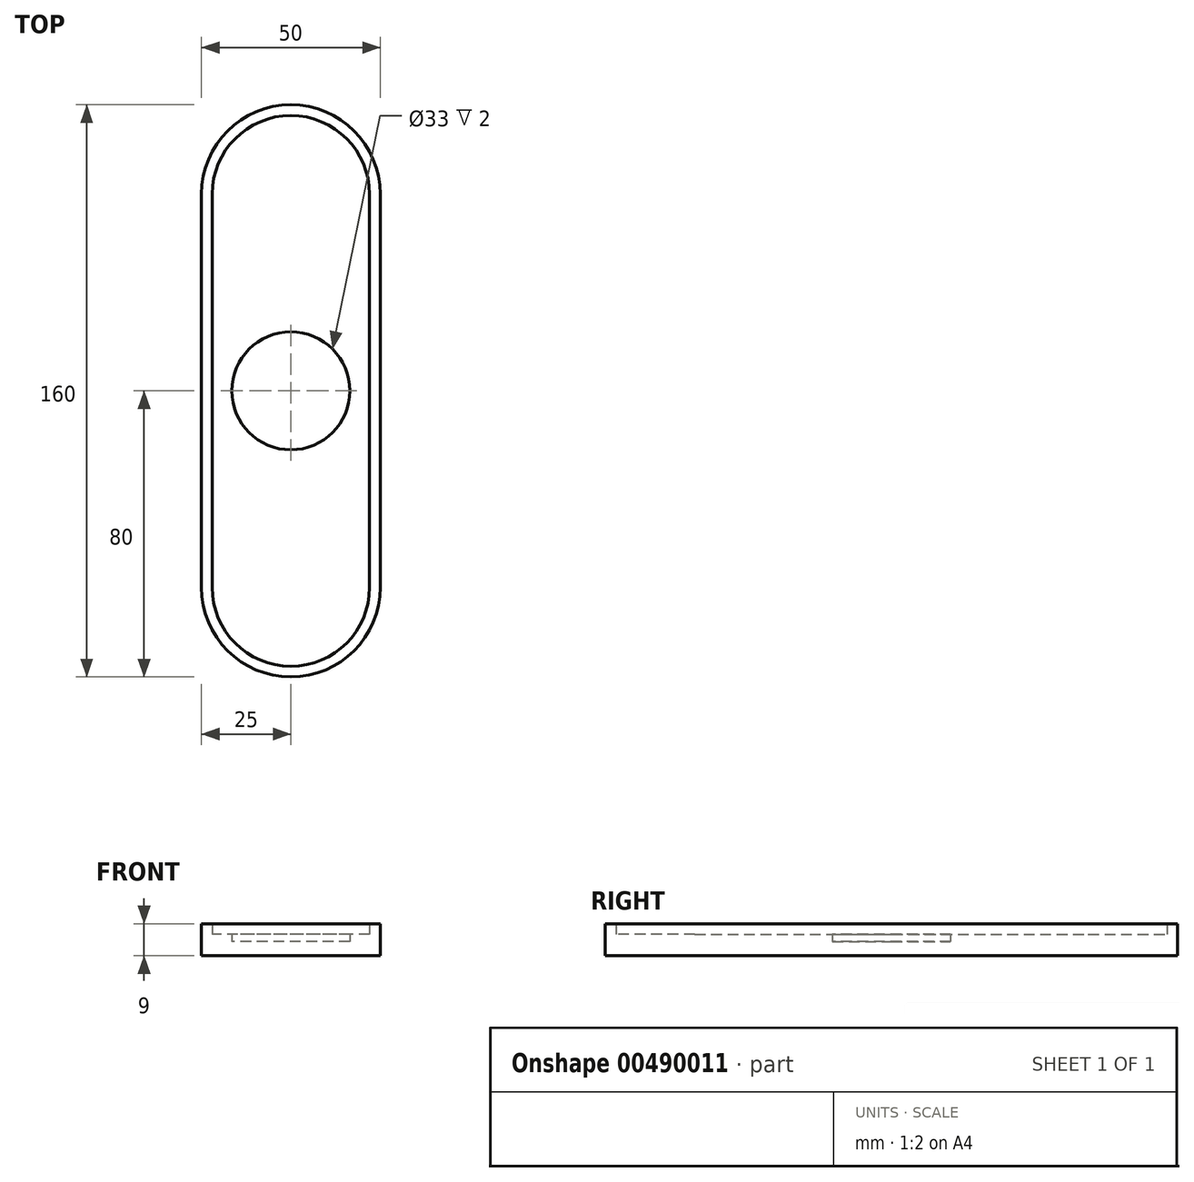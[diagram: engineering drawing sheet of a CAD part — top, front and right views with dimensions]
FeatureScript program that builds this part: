
annotation { "Feature Type Name" : "Feature", "Feature Type Description" : "" }
export const myFeature = defineFeature(function(context is Context, id is Id, definition is map)
    precondition{}
    {
        {
            var Q0;
            Q0=qCreatedBy(makeId("Top.planeOp"),FACE);
            var sketch = newSketch(context, id + "F0", { "sketchPlane" : qUnion([Q0])});
            skLineSegment(sketch, "E0.bottom", {"start": v(0, -80) * mm, "end": v(0, -80) * mm});
            skLineSegment(sketch, "E0.top", {"start": v(0, 80) * mm, "end": v(0, 80) * mm});
            skLineSegment(sketch, "E0.left", {"start": v(25, -55) * mm, "end": v(25, 55) * mm});
            skLineSegment(sketch, "E0.right", {"start": v(-25, -55) * mm, "end": v(-25, 55) * mm});
            skPoint(sketch, "E0.middle", {"position": v(0, 0) * mm});
            skLineSegment(sketch, "E1.0", {"start": v(0, 77) * mm, "end": v(0, 77) * mm});
            skLineSegment(sketch, "E1.1", {"start": v(22, -55) * mm, "end": v(22, 55) * mm});
            skLineSegment(sketch, "E1.2", {"start": v(0, -77) * mm, "end": v(0, -77) * mm});
            skLineSegment(sketch, "E1.3", {"start": v(-22, -55) * mm, "end": v(-22, 55) * mm});
            skCircle(sketch, "E2", {"center": v(0, 0) * mm, "radius": 16.5 * mm});
            skCircle(sketch, "E3.1.0.0", {"center": v(0, 45) * mm, "radius": 16.5 * mm});
            skLineSegment(sketch, "E3.direction1", {"start": v(0, 0) * mm, "end": v(0, 45) * mm, "construction": true});
            skCircle(sketch, "E4", {"center": v(0, -45) * mm, "radius": 15 * mm});
            skPoint(sketch, "E5.visualSharp", {"position": v(-22, 77) * mm});
            skArc(sketch, "E5.filletArc", {"start": v(0, 77) * mm, "mid": v(-15.56, 70.56) * mm, "end": v(-22, 55) * mm});
            skPoint(sketch, "E6.visualSharp", {"position": v(22, 77) * mm});
            skArc(sketch, "E6.filletArc", {"start": v(22, 55) * mm, "mid": v(15.56, 70.56) * mm, "end": v(0, 77) * mm});
            skPoint(sketch, "E7.visualSharp", {"position": v(-22, -77) * mm});
            skArc(sketch, "E7.filletArc", {"start": v(-22, -55) * mm, "mid": v(-15.56, -70.56) * mm, "end": v(0, -77) * mm});
            skPoint(sketch, "E8.visualSharp", {"position": v(22, -77) * mm});
            skArc(sketch, "E8.filletArc", {"start": v(0, -77) * mm, "mid": v(15.56, -70.56) * mm, "end": v(22, -55) * mm});
            skPoint(sketch, "E9.visualSharp", {"position": v(-25, 80) * mm});
            skArc(sketch, "E9.filletArc", {"start": v(0, 80) * mm, "mid": v(-17.68, 72.68) * mm, "end": v(-25, 55) * mm});
            skPoint(sketch, "E10.visualSharp", {"position": v(25, 80) * mm});
            skArc(sketch, "E10.filletArc", {"start": v(25, 55) * mm, "mid": v(17.68, 72.68) * mm, "end": v(0, 80) * mm});
            skPoint(sketch, "E11.visualSharp", {"position": v(-25, -80) * mm});
            skArc(sketch, "E11.filletArc", {"start": v(-25, -55) * mm, "mid": v(-17.68, -72.68) * mm, "end": v(0, -80) * mm});
            skPoint(sketch, "E12.visualSharp", {"position": v(25, -80) * mm});
            skArc(sketch, "E12.filletArc", {"start": v(0, -80) * mm, "mid": v(17.68, -72.68) * mm, "end": v(25, -55) * mm});
            skSolve(sketch);
        }
        {
            var Q0;
            Q0=makeQuery(id+"F0.imprint","IMPRINT",FACE,{"disambiguationData":[TD([[makeQuery(id+"F0.imprint","IMPRINT",EDGE,{"derivedFrom":sQuery(id+"F0.wireOp",EDGE,"E1.1")}),1.0]])]});
            var Q1;
            Q1=makeQuery(id+"F0.imprint","IMPRINT",FACE,{"disambiguationData":[TD([[makeQuery(id+"F0.imprint","IMPRINT",EDGE,{"derivedFrom":sQuery(id+"F0.wireOp",EDGE,"E4")}),1.0]])]});
            var Q2;
            Q2=makeQuery(id+"F0.imprint","IMPRINT",FACE,{"disambiguationData":[TD([[makeQuery(id+"F0.imprint","IMPRINT",EDGE,{"derivedFrom":sQuery(id+"F0.wireOp",EDGE,"E3.1.0.0")}),1.0]])]});
            extrude(context, id + "F1", {"entities" : qUnion([Q0, Q1, Q2]), "depth" : 6 * mm});
        }
        {
            var Q0;
            Q0=makeQuery(id+"F0.imprint","IMPRINT",FACE,{"disambiguationData":[TD([[makeQuery(id+"F0.imprint","IMPRINT",EDGE,{"derivedFrom":sQuery(id+"F0.wireOp",EDGE,"E4")}),1.0]])]});
            var Q1;
            Q1=makeQuery(id+"F0.imprint","IMPRINT",FACE,{"disambiguationData":[TD([[makeQuery(id+"F0.imprint","IMPRINT",EDGE,{"derivedFrom":sQuery(id+"F0.wireOp",EDGE,"E2")}),1.0]])]});
            var Q2;
            Q2=makeQuery(id+"F0.imprint","IMPRINT",FACE,{"disambiguationData":[TD([[makeQuery(id+"F0.imprint","IMPRINT",EDGE,{"derivedFrom":sQuery(id+"F0.wireOp",EDGE,"E3.1.0.0")}),1.0]])]});
            extrude(context, id + "F2", {"entities" : qUnion([Q0, Q1, Q2]), "operationType" : NewBodyOperationType.ADD, "depth" : 4 * mm});
        }
        {
            var Q0;
            Q0=makeQuery(id+"F0.imprint","IMPRINT",FACE,{"disambiguationData":[TD([[makeQuery(id+"F0.imprint","IMPRINT",EDGE,{"derivedFrom":sQuery(id+"F0.wireOp",EDGE,"E0.left")}),1.0]])]});
            extrude(context, id + "F3", {"entities" : qUnion([Q0]), "operationType" : NewBodyOperationType.ADD, "depth" : 9 * mm});
        }
    });
